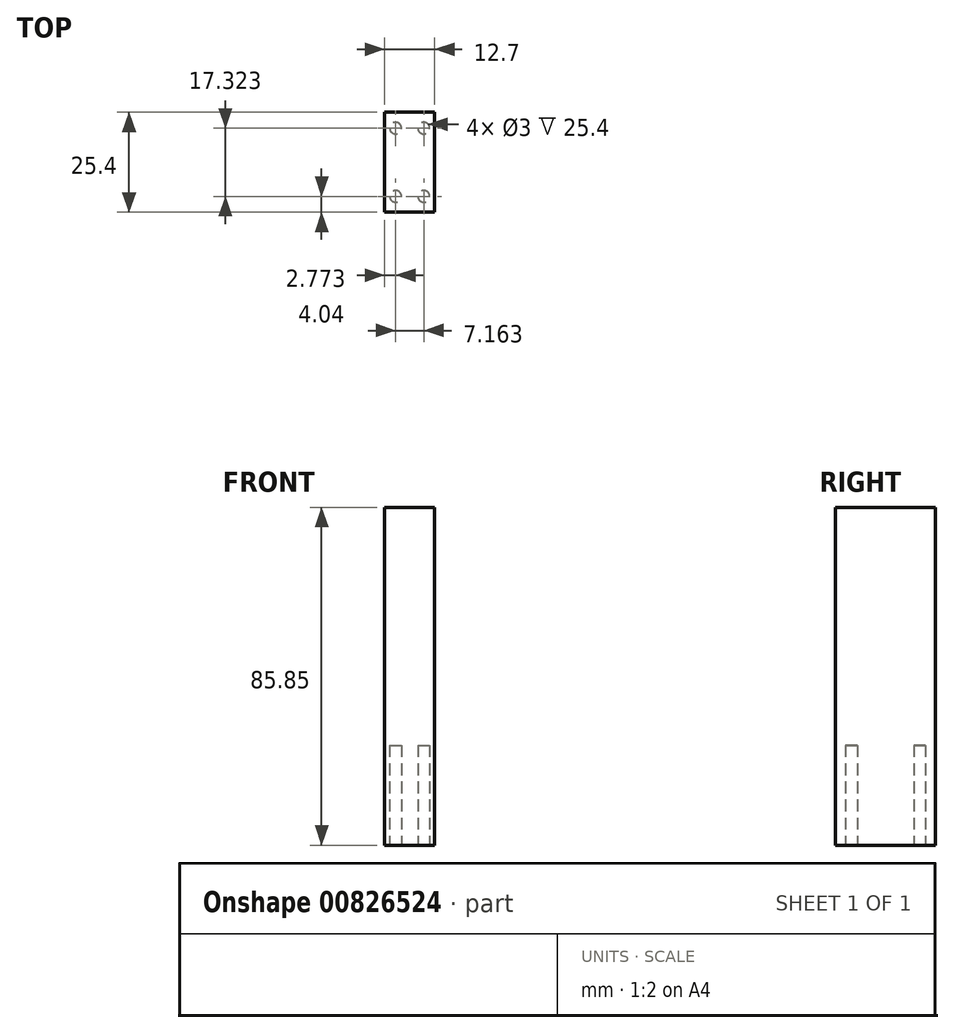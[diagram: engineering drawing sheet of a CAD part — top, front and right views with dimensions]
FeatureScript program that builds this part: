
annotation { "Feature Type Name" : "Feature", "Feature Type Description" : "" }
export const myFeature = defineFeature(function(context is Context, id is Id, definition is map)
    precondition{}
    {
        {
            var Q0;
            Q0=qCreatedBy(makeId("Top.planeOp"),FACE);
            var sketch = newSketch(context, id + "F0", { "sketchPlane" : qUnion([Q0])});
            skLineSegment(sketch, "E0", {"start": v(-19.72, -19) * mm, "end": v(-19.72, 6.4) * mm});
            skLineSegment(sketch, "E1", {"start": v(-19.72, 6.4) * mm, "end": v(-7.02, 6.4) * mm});
            skLineSegment(sketch, "E2", {"start": v(-7.02, 6.4) * mm, "end": v(-7.02, -19) * mm});
            skLineSegment(sketch, "E3", {"start": v(-19.72, -19) * mm, "end": v(-7.02, -19) * mm});
            skSolve(sketch);
        }
        {
            var Q0;
            Q0=makeQuery(id+"F0.imprint","IMPRINT",FACE,{"disambiguationData":[TD([[makeQuery(id+"F0.imprint","IMPRINT",EDGE,{"derivedFrom":sQuery(id+"F0.wireOp",EDGE,"E0")}),-1.0]])]});
            extrude(context, id + "F1", {"entities" : qUnion([Q0]), "depth" : 85.85 * mm, "offsetDistance" : 25.4 * mm});
        }
        {
            assignVariable(context, id + "F2", {"name" : "LR_screwDepth", "anyValue" : 25.4 * mm});
        }
        {
            var Q0;
            Q0=makeQuery(id+"F1.opExtrude","CAP_FACE",FACE,{"disambiguationData":[OSD([sQuery(id+"F0.wireOp",EDGE,"E0"),sQuery(id+"F0.wireOp",EDGE,"E1"),sQuery(id+"F0.wireOp",EDGE,"E2"),sQuery(id+"F0.wireOp",EDGE,"E3")])],"isStart":true});
            var sketch = newSketch(context, id + "F3", { "sketchPlane" : qUnion([Q0])});
            skLineSegment(sketch, "E4.bottom", {"start": v(-16.95, -2.36) * mm, "end": v(-9.78, -2.36) * mm, "construction": true});
            skLineSegment(sketch, "E4.top", {"start": v(-16.95, 14.96) * mm, "end": v(-9.78, 14.96) * mm, "construction": true});
            skLineSegment(sketch, "E4.right", {"start": v(-9.78, -2.36) * mm, "end": v(-9.78, 14.96) * mm, "construction": true});
            skLineSegment(sketch, "E5", {"start": v(-7.02, 6.3) * mm, "end": v(-9.78, 6.3) * mm, "construction": true});
            skPoint(sketch, "E5.startSnap0", {"position": v(-7.02, 6.3) * mm});
            skLineSegment(sketch, "E6", {"start": v(-13.37, -2.36) * mm, "end": v(-13.37, -6.4) * mm, "construction": true});
            skCircle(sketch, "E7", {"center": v(-16.95, -2.36) * mm, "radius": 1.5 * mm});
            skCircle(sketch, "E8", {"center": v(-9.78, -2.36) * mm, "radius": 1.5 * mm});
            skCircle(sketch, "E9", {"center": v(-16.95, 14.96) * mm, "radius": 1.5 * mm});
            skCircle(sketch, "E10", {"center": v(-9.78, 14.96) * mm, "radius": 1.5 * mm});
            skLineSegment(sketch, "E11", {"start": v(-13.37, 14.96) * mm, "end": v(-13.37, 19) * mm, "construction": true});
            skSolve(sketch);
        }
        {
            var Q0;
            Q0=qSketchRegion(id+"F3",true);
            extrude(context, id + "F4", {"entities" : qUnion([Q0]), "operationType" : NewBodyOperationType.REMOVE, "oppositeDirection" : true, "depth" : getVariable(context, 'LR_screwDepth'), "offsetDistance" : 25.4 * mm});
        }
    });
